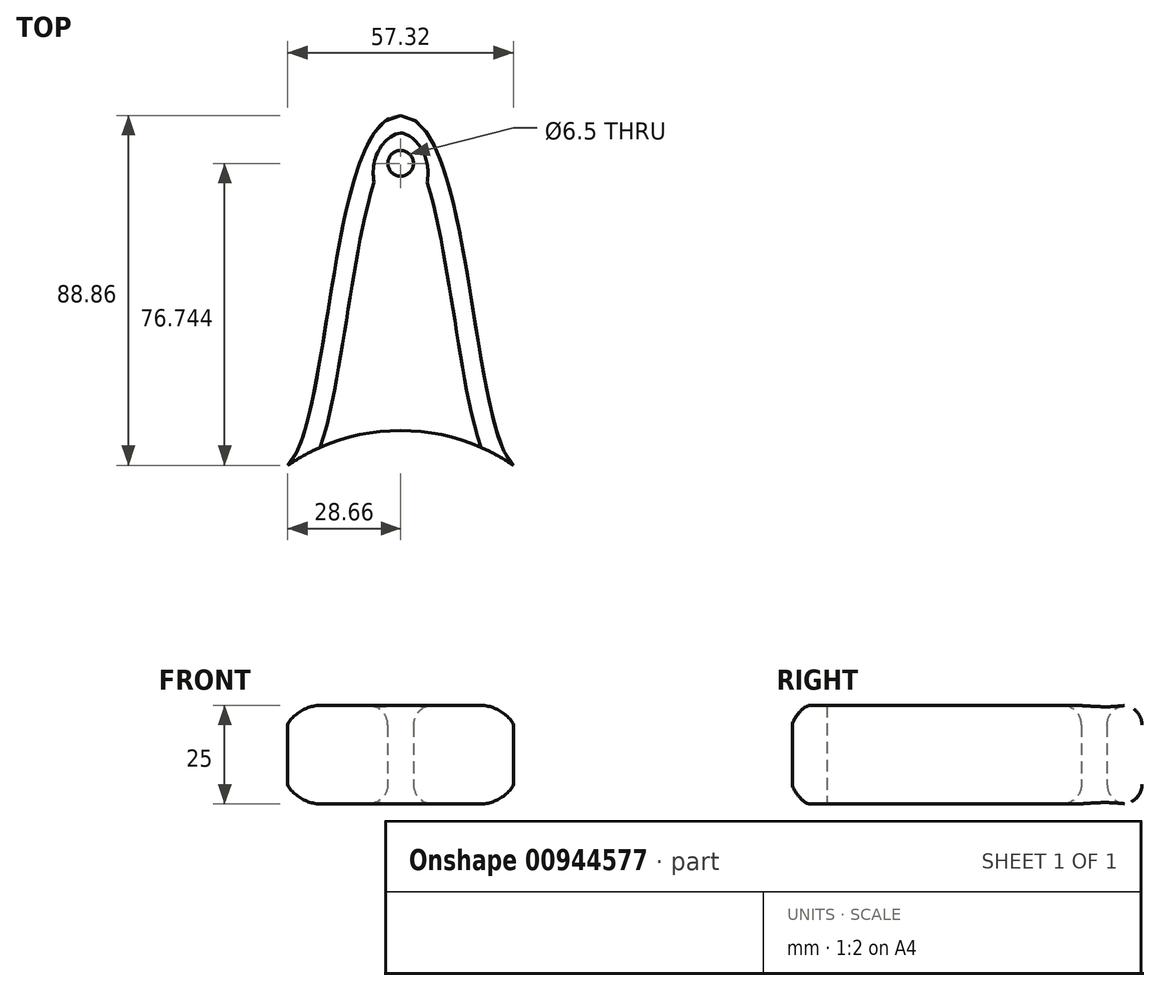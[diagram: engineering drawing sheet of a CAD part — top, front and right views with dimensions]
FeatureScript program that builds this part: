
annotation { "Feature Type Name" : "Feature", "Feature Type Description" : "" }
export const myFeature = defineFeature(function(context is Context, id is Id, definition is map)
    precondition{}
    {
        {
            var Q0;
            Q0=qCreatedBy(makeId("Top.planeOp"),FACE);
            var sketch = newSketch(context, id + "F0", { "sketchPlane" : qUnion([Q0])});
            skCircle(sketch, "E0", {"center": v(0, 0) * mm, "radius": 50.8 * mm});
            skLineSegment(sketch, "E1", {"start": v(0, 0) * mm, "end": v(0, 50.8) * mm});
            skLineSegment(sketch, "E2", {"start": v(0, 50.8) * mm, "end": v(0, 130.8) * mm});
            skLineSegment(sketch, "E3", {"start": v(0, 50.8) * mm, "end": v(28.66, 41.94) * mm});
            skFitSpline(sketch, "E4", {"points": [v(28.66, 41.94) * mm, v(0, 130.8) * mm], "startDerivative": vector(-33.05, 30.59) * mm, "endDerivative": vector(-54.25, 0) * mm});
            skFitSpline(sketch, "E5.MirrorCS", {"points": [v(-28.66, 41.94) * mm, v(0, 130.8) * mm], "startDerivative": vector(33.05, 30.59) * mm, "endDerivative": vector(54.25, 0) * mm});
            skCircle(sketch, "E6", {"center": v(0, 118.68) * mm, "radius": 3.25 * mm});
            skSolve(sketch);
        }
        {
            var Q0;
            {var subQ0=sQuery(id+"F0.wireOp",EDGE,"E5.MirrorCS");Q0=makeQuery(id+"F0.imprint","IMPRINT",FACE,{"disambiguationData":[TD([[makeQuery(id+"F0.imprint","IMPRINT",EDGE,{"derivedFrom":subQ0}),-1.0]])]});}
            var Q1;
            {var subQ0=sQuery(id+"F0.wireOp",EDGE,"E4");Q1=makeQuery(id+"F0.imprint","IMPRINT",FACE,{"disambiguationData":[TD([[makeQuery(id+"F0.imprint","IMPRINT",EDGE,{"derivedFrom":subQ0}),1.0]])]});}
            extrude(context, id + "F1", {"entities" : qUnion([Q0, Q1]), "depth" : 25 * mm, "offsetDistance" : 25 * mm});
        }
        {
            var Q0;
            Q0=makeQuery(id+"F1.opExtrude","CAP_EDGE",EDGE,{"disambiguationData":[OSD([sQuery(id+"F0.wireOp",EDGE,"E4")])],"isStart":true});
            var Q1;
            Q1=makeQuery(id+"F1.opExtrude","CAP_EDGE",EDGE,{"disambiguationData":[OSD([sQuery(id+"F0.wireOp",EDGE,"E4")])],"isStart":false});
            var Q2;
            Q2=makeQuery(id+"F1.opExtrude","CAP_EDGE",EDGE,{"disambiguationData":[OSD([sQuery(id+"F0.wireOp",EDGE,"E5.MirrorCS")])],"isStart":true});
            var Q3;
            Q3=makeQuery(id+"F1.opExtrude","CAP_EDGE",EDGE,{"disambiguationData":[OSD([sQuery(id+"F0.wireOp",EDGE,"E5.MirrorCS")])],"isStart":false});
            var Q4;
            Q4=makeQuery(id+"F1.opExtrude","CAP_EDGE",EDGE,{"disambiguationData":[OSD([sQuery(id+"F0.wireOp",EDGE,"E6")])],"isStart":false});
            var Q5;
            Q5=makeQuery(id+"F1.opExtrude","CAP_EDGE",EDGE,{"disambiguationData":[OSD([sQuery(id+"F0.wireOp",EDGE,"E6")])],"isStart":true});
            fillet(context, id + "F2", {"entities" : qUnion([Q0, Q1, Q2, Q3, Q4, Q5]), "radius" : 5 * mm, "tangentPropagation" : true, "allowEdgeOverflow" : false});
        }
    });
